# Revit family: OXYTYP003
name_source: partatom
category: Furniture
units: mm (PartAtom-declared; Revit-internal decimal feet)

## family parameters
Always vertical = Yes
Cut with Voids When Loaded = No
OmniClass Number = 23.40.20.00
OmniClass Title = General Furniture and Specialties
Render Appearance Source = Family Geometry
Room Calculation Point = No
Shared = No
Work Plane-Based = No

## types (1)
- OXYTYP003
    Cost = 36125 $
    Default Elevation = 0 mm  [stored 0 ft]
    Description = 4 x Chelsea Task, Black Mesh Back, Black Fab Seat w/White Frame, 4 x Desktop Organizer - White, 2 x PET Sling for 24D Surface 14Hx8Wx18D, 2 x Duplex Outlet - Line 1 - Black, 2 x Duplex Outlet - Line 2 - Black, 2 x Duplex Outlet - Line 3 - Black, 2 x Duplex Outlet - Line 4 Dedicated - Black, 1 x 51 in. Electrical Jumper (Pt 30E), 1 x Unv. Spine Insert Screen - Glass .250 16H x 48W, 1 x Base Infeed - with Pole - 8 Wire 4 Circuit - Side Mounted, 2 x Double Bench Powered w/Access Boxes 48D X 72W, 2 x End Cap - Flat EC for Straight Legs - 48, 2 x Slimline Scrn,Uni Spine,FVWL,Dim A,SpnMntUni,16hx48w, 1 x Double Sided Shared Straight Leg Kit - 48D, 2 x Double Sided Straight Leg Kit - 48D, 2 x Desking L-Bracket Pair (2) Black Brackets, 2 x Worksurface - Oxygen Return Rectangular - 24D x 23.75W, 6 x Flat Plate, 1 x CBX Single Door Locker Left 50h x 12w x 24d, 1 x CBX BBF Ped Tower with Open Side RH 24Dx50Hx12W, 1 x Cbx Shared Lateral With Sliding Door Rh 18dx50hx36w
    Exported From CET Designer = Yes
    Manufacturer = AIS
    Model = 5100
    Show OXYTYP003 = Yes
    VisibilityIndex = 0

note: [stored X ft] marks values corroborated as IEEE doubles in the binary element streams (Revit-internal decimal feet)

## geometry (parser evidence)
native form markers: Sweep x3
no freeform markers — native parametric forms only
